# Revit family: LCAT-CM
name_source: partatom
category: Lighting Fixtures
units: mm (PartAtom-declared; Revit-internal decimal feet)

## family parameters
Cut with Voids When Loaded = No
Host = Face
Light Source = No
OmniClass Number = 23.80.70.11
OmniClass Title = Luminaries for Internal Lighting
Part Type = Normal
Room Calculation Point = No
Round Connector Dimension = Use Diameter
Shared = No

## types (3) — shared parameters
Apparent Load = 0 VA
Backbox = White
Default Elevation = 4.000'
Description = LCAT provides both design and value with an architectural appearance, LED technology to reduce maintenance and a wide range of options for classrooms, offices, retail and health care applications
Lamp = LED Lamp
Light Bulb = White Glass
Manufacturer = Columbia Lighting
Suspension Height = 2.000'
URL = https://www.currentlighting.com
Voltage = 120 V
Warranty = Five year warranty
Wattage Comments = 40-80 W

## per-type parameters (varying)
| type | Load Classification | Photometric Web | Row Length | Width | zz Length |
| LCAT-CM-14 | Lighting | Web LCAT : LCAT14-30HLG-EDU | 4.000' | 1.000' | 3.917' |
| LCAT-CM-22 | Other | Web LCAT : LCAT22-50HLG-EDU | 2.000' | 1.979' | 1.917' |
| LCAT-CM-24 | Lighting | Web LCAT : LCAT24-35LWG-EDU | 4.000' | 2.083' | 3.917' |

note: column(s) folded — value = type name in every type: Model

## geometry (parser evidence)
native form markers: Sweep x6
no freeform markers — native parametric forms only
